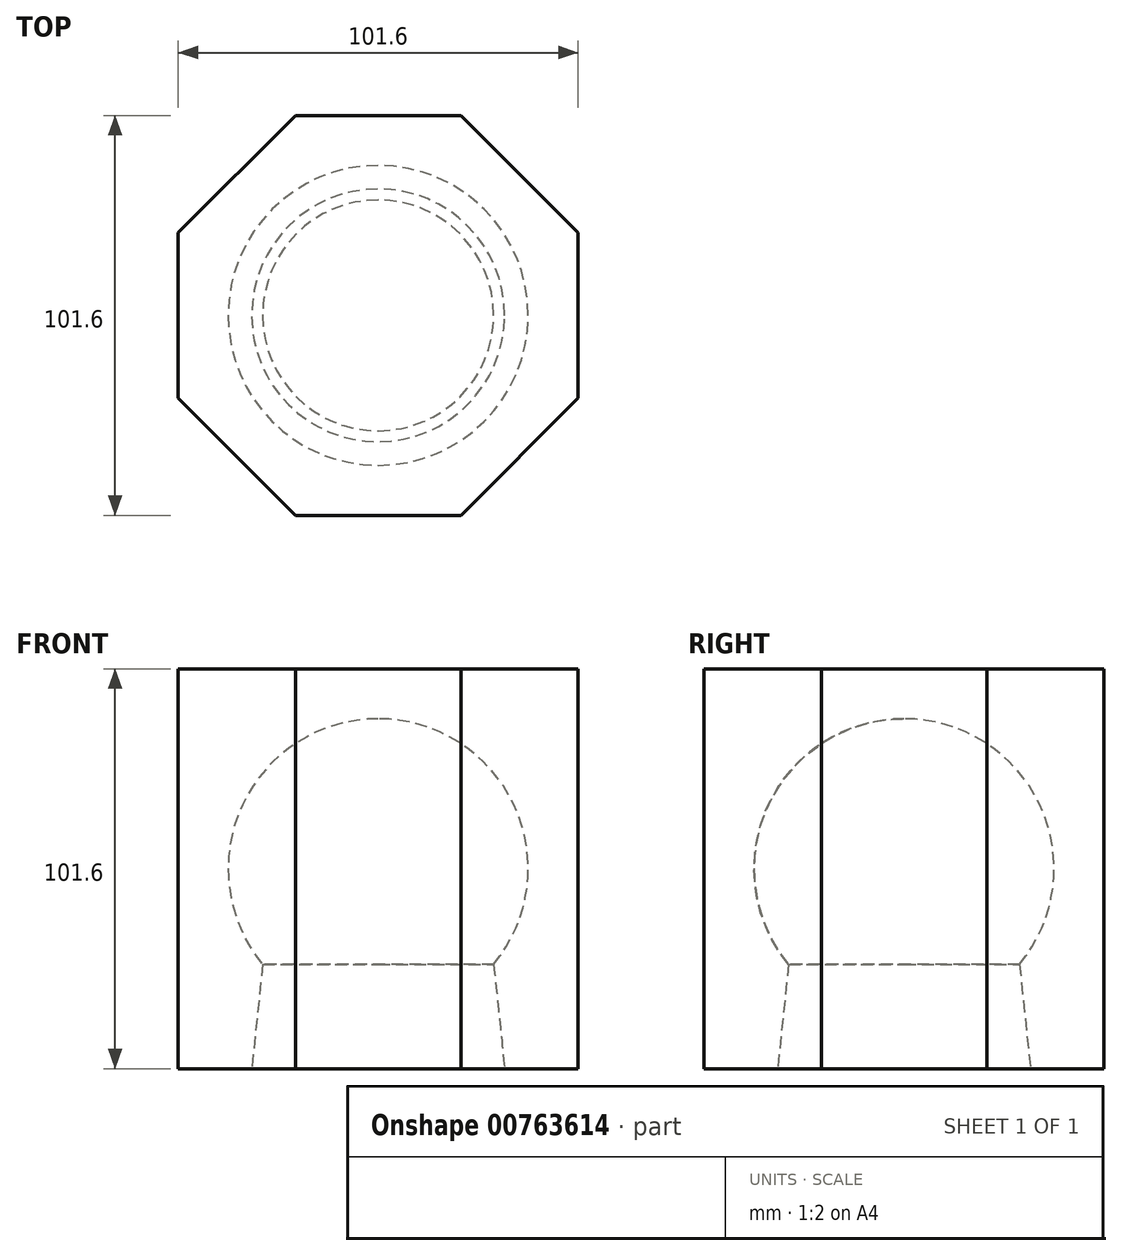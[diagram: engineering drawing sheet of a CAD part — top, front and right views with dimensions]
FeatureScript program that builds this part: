
annotation { "Feature Type Name" : "Feature", "Feature Type Description" : "" }
export const myFeature = defineFeature(function(context is Context, id is Id, definition is map)
    precondition{}
    {
        {
            var Q0;
            Q0=qCreatedBy(makeId("Top.planeOp"),FACE);
            var sketch = newSketch(context, id + "F0", { "sketchPlane" : qUnion([Q0])});
            skCircle(sketch, "E0.cCircle", {"center": v(0, 0) * mm, "radius": 50.8 * mm, "construction": true});
            skLineSegment(sketch, "E0.0", {"start": v(21.04, -50.8) * mm, "end": v(-21.04, -50.8) * mm});
            skLineSegment(sketch, "E0.1", {"start": v(-21.04, -50.8) * mm, "end": v(-50.8, -21.04) * mm});
            skLineSegment(sketch, "E0.2", {"start": v(-50.8, -21.04) * mm, "end": v(-50.8, 21.04) * mm});
            skLineSegment(sketch, "E0.3", {"start": v(-50.8, 21.04) * mm, "end": v(-21.04, 50.8) * mm});
            skLineSegment(sketch, "E0.4", {"start": v(-21.04, 50.8) * mm, "end": v(21.04, 50.8) * mm});
            skLineSegment(sketch, "E0.5", {"start": v(21.04, 50.8) * mm, "end": v(50.8, 21.04) * mm});
            skLineSegment(sketch, "E0.6", {"start": v(50.8, 21.04) * mm, "end": v(50.8, -21.04) * mm});
            skLineSegment(sketch, "E0.7", {"start": v(50.8, -21.04) * mm, "end": v(21.04, -50.8) * mm});
            skPoint(sketch, "E0.0.midPoint", {"position": v(0, -50.8) * mm});
            skSolve(sketch);
        }
        {
            var Q0;
            Q0=makeQuery(id+"F0.imprint","IMPRINT",FACE,{"disambiguationData":[TD([[makeQuery(id+"F0.imprint","IMPRINT",EDGE,{"derivedFrom":sQuery(id+"F0.wireOp",EDGE,"E0.0")}),-1.0]])]});
            extrude(context, id + "F1", {"entities" : qUnion([Q0]), "depth" : 101.6 * mm, "offsetDistance" : 25.4 * mm});
        }
        {
            var Q0;
            Q0=qCreatedBy(makeId("Right.planeOp"),FACE);
            var sketch = newSketch(context, id + "F2", { "sketchPlane" : qUnion([Q0])});
            skLineSegment(sketch, "E1", {"start": v(0, 0) * mm, "end": v(0, 88.9) * mm});
            skArc(sketch, "E2", {"start": v(0, 88.9) * mm, "mid": v(-34.48, 67) * mm, "end": v(-29.34, 26.5) * mm});
            skLineSegment(sketch, "E3", {"start": v(-32.13, 0) * mm, "end": v(-29.34, 26.5) * mm});
            skLineSegment(sketch, "E4", {"start": v(-32.13, 0) * mm, "end": v(0, 0) * mm});
            skLineSegment(sketch, "E5", {"start": v(0, 0) * mm, "end": v(0, -82) * mm, "construction": true});
            skLineSegment(sketch, "E6", {"start": v(0, -82) * mm, "end": v(0, -82) * mm});
            skLineSegment(sketch, "E7", {"start": v(-40.77, -82) * mm, "end": v(0, -82) * mm, "construction": true});
            skLineSegment(sketch, "E8", {"start": v(-32.13, 0) * mm, "end": v(-40.77, -82) * mm, "construction": true});
            skSolve(sketch);
        }
        {
            var Q0;
            Q0=makeQuery(id+"F2.imprint","IMPRINT",FACE,{"disambiguationData":[TD([[makeQuery(id+"F2.imprint","IMPRINT",EDGE,{"derivedFrom":sQuery(id+"F2.wireOp",EDGE,"E1")}),1.0]])]});
            var Q1;
            Q1=sQuery(id+"F2.wireOp",EDGE,"E1");
            revolve(context, id + "F3", {"operationType" : NewBodyOperationType.REMOVE, "surfaceOperationType" : NewSurfaceOperationType.NEW, "entities" : qUnion([Q0]), "axis" : qUnion([Q1]), "revolveType" : RevolveType.FULL, "oppositeDirection" : true});
        }
    });
